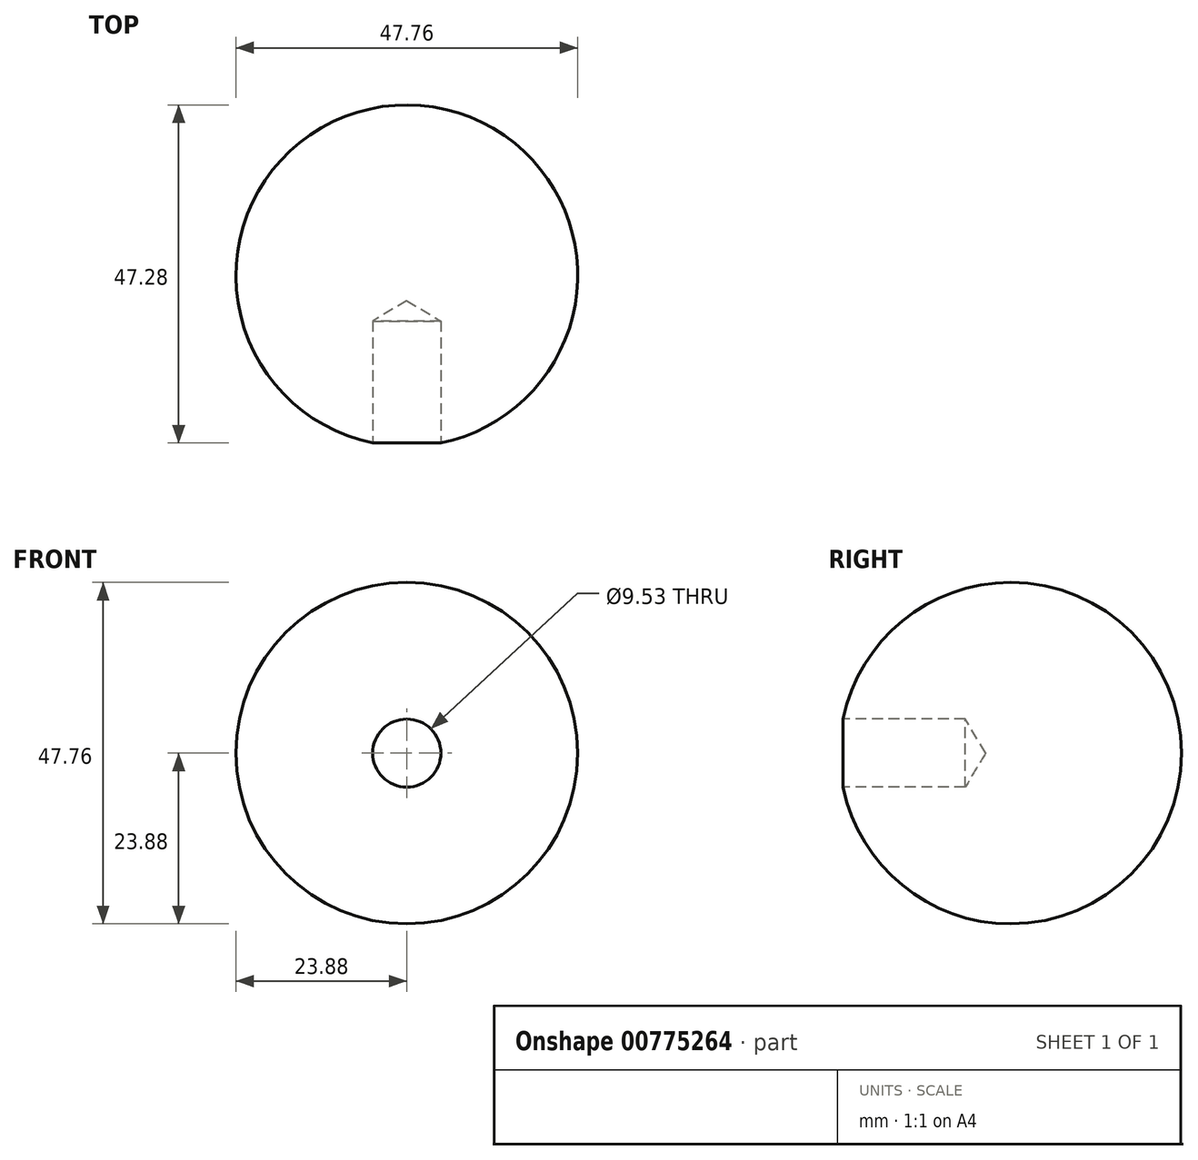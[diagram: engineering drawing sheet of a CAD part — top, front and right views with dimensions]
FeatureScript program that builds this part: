
annotation { "Feature Type Name" : "Feature", "Feature Type Description" : "" }
export const myFeature = defineFeature(function(context is Context, id is Id, definition is map)
    precondition{}
    {
        {
            var Q0;
            Q0=qCreatedBy(makeId("Front.planeOp"),FACE);
            var sketch = newSketch(context, id + "F0", { "sketchPlane" : qUnion([Q0])});
            skArc(sketch, "E0", {"start": v(0, -23.88) * mm, "mid": v(23.88, 0) * mm, "end": v(0, 23.88) * mm});
            skLineSegment(sketch, "E1", {"start": v(0, 0) * mm, "end": v(23.88, 0) * mm, "construction": true});
            skLineSegment(sketch, "E2", {"start": v(0, 23.88) * mm, "end": v(0, -23.88) * mm});
            skSolve(sketch);
        }
        {
            var Q0;
            Q0 = qSketchRegion(id + "F0", true);
            var Q1;
            Q1=sQuery(id+"F0.wireOp",EDGE,"E2");
            revolve(context, id + "F1", {"surfaceOperationType" : NewSurfaceOperationType.NEW, "entities" : qUnion([Q0]), "axis" : qUnion([Q1]), "revolveType" : RevolveType.FULL});
        }
        {
            var Q0;
            Q0=qCreatedBy(makeId("Front.planeOp"),FACE);
            cPlane(context, id + "F2", {"entities" : qUnion([Q0]), "cplaneType" : CPlaneType.OFFSET, "offset" : 25.4 * mm, "width" : 152.4 * mm, "height" : 152.4 * mm});
        }
        {
            var Q0;
            Q0=qCreatedBy(id+"F2.planeOp",FACE);
            var sketch = newSketch(context, id + "F3", { "sketchPlane" : qUnion([Q0])});
            skPoint(sketch, "E3", {"position": v(0, 0) * mm});
            skSolve(sketch);
        }
        {
            var Q0;
            Q0=sQuery(id+"F3.wireOp",VERTEX,"E3");
            var Q1;
            Q1=makeQuery(id+"F1.opRevolve","SWEPT_BODY",BODY,{"disambiguationData":[OSD([sQuery(id+"F0.wireOp",EDGE,"E0"),sQuery(id+"F0.wireOp",EDGE,"E2")])]});
            hole(context, id + "F4", {"style" : HoleStyle.SIMPLE, "endStyle" : HoleEndStyle.BLIND, "holeDiameter" : 9.52 * mm, "majorDiameter" : 6.35 * mm, "holeDepth" : 19.05 * mm, "isTappedThrough" : true, "tappedDepth" : 12.7 * mm, "tapClearance" : 3, "startFromSketch" : true, "locations" : qUnion([Q0]), "scope" : qUnion([Q1])});
        }
    });
